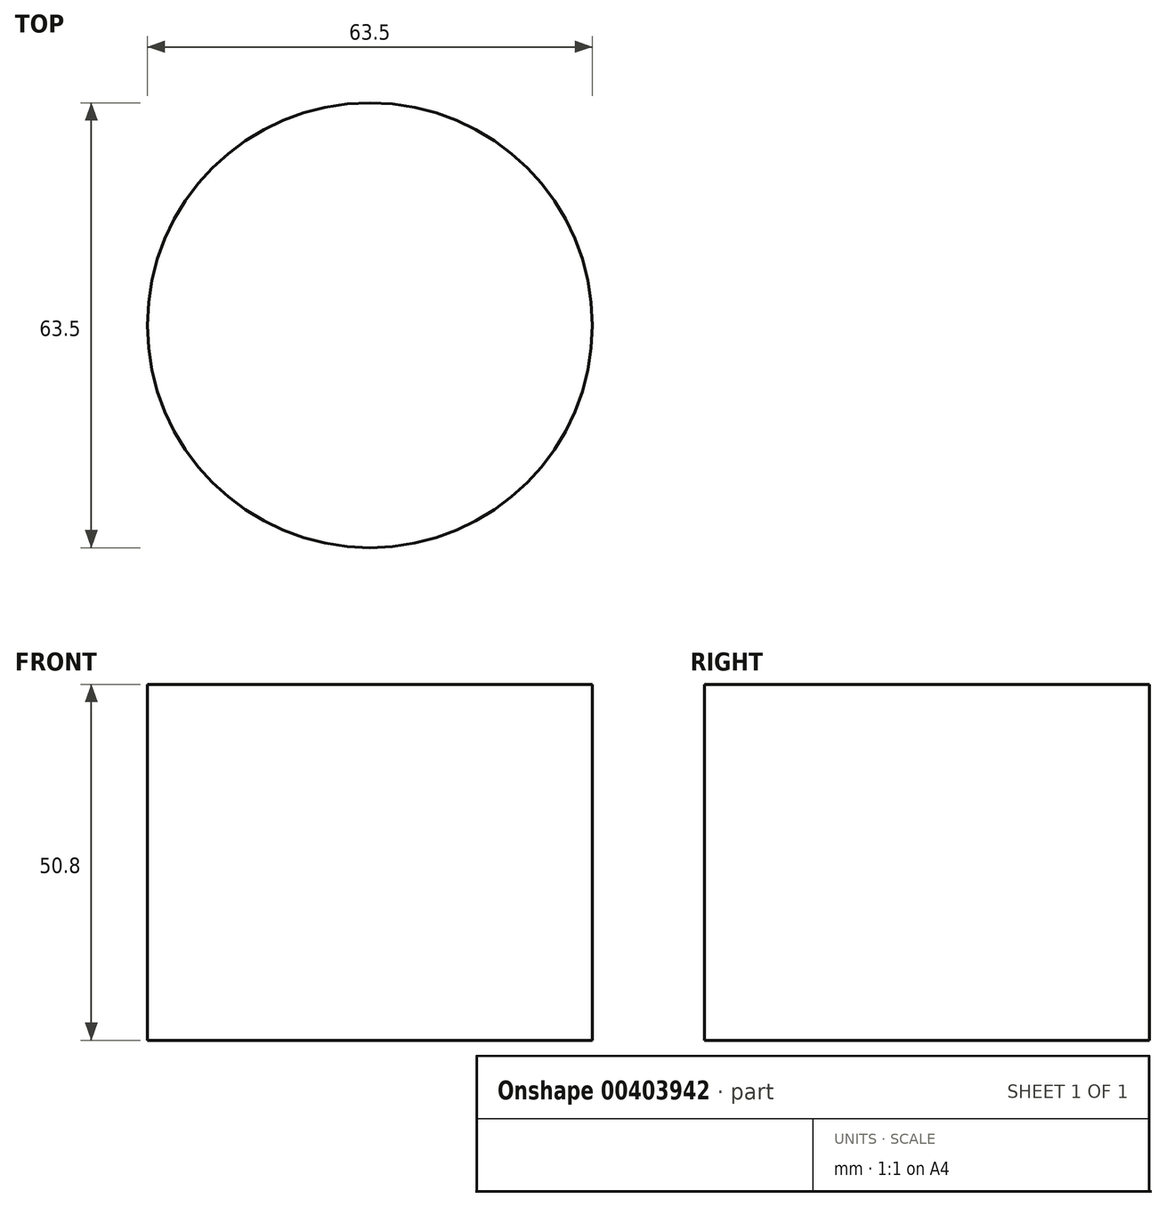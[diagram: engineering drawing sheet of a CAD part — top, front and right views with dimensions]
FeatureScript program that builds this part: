
annotation { "Feature Type Name" : "Feature", "Feature Type Description" : "" }
export const myFeature = defineFeature(function(context is Context, id is Id, definition is map)
    precondition{}
    {
        {
            var Q0;
            Q0=qCreatedBy(makeId("Top.planeOp"),FACE);
            var sketch = newSketch(context, id + "F0", { "sketchPlane" : qUnion([Q0])});
            skCircle(sketch, "E0", {"center": v(0, 0) * mm, "radius": 31.75 * mm});
            skSolve(sketch);
        }
        {
            var Q0;
            Q0 = qSketchRegion(id + "F0", true);
            extrude(context, id + "F1", {"entities" : qUnion([Q0]), "depth" : 50.8 * mm});
        }
    });
